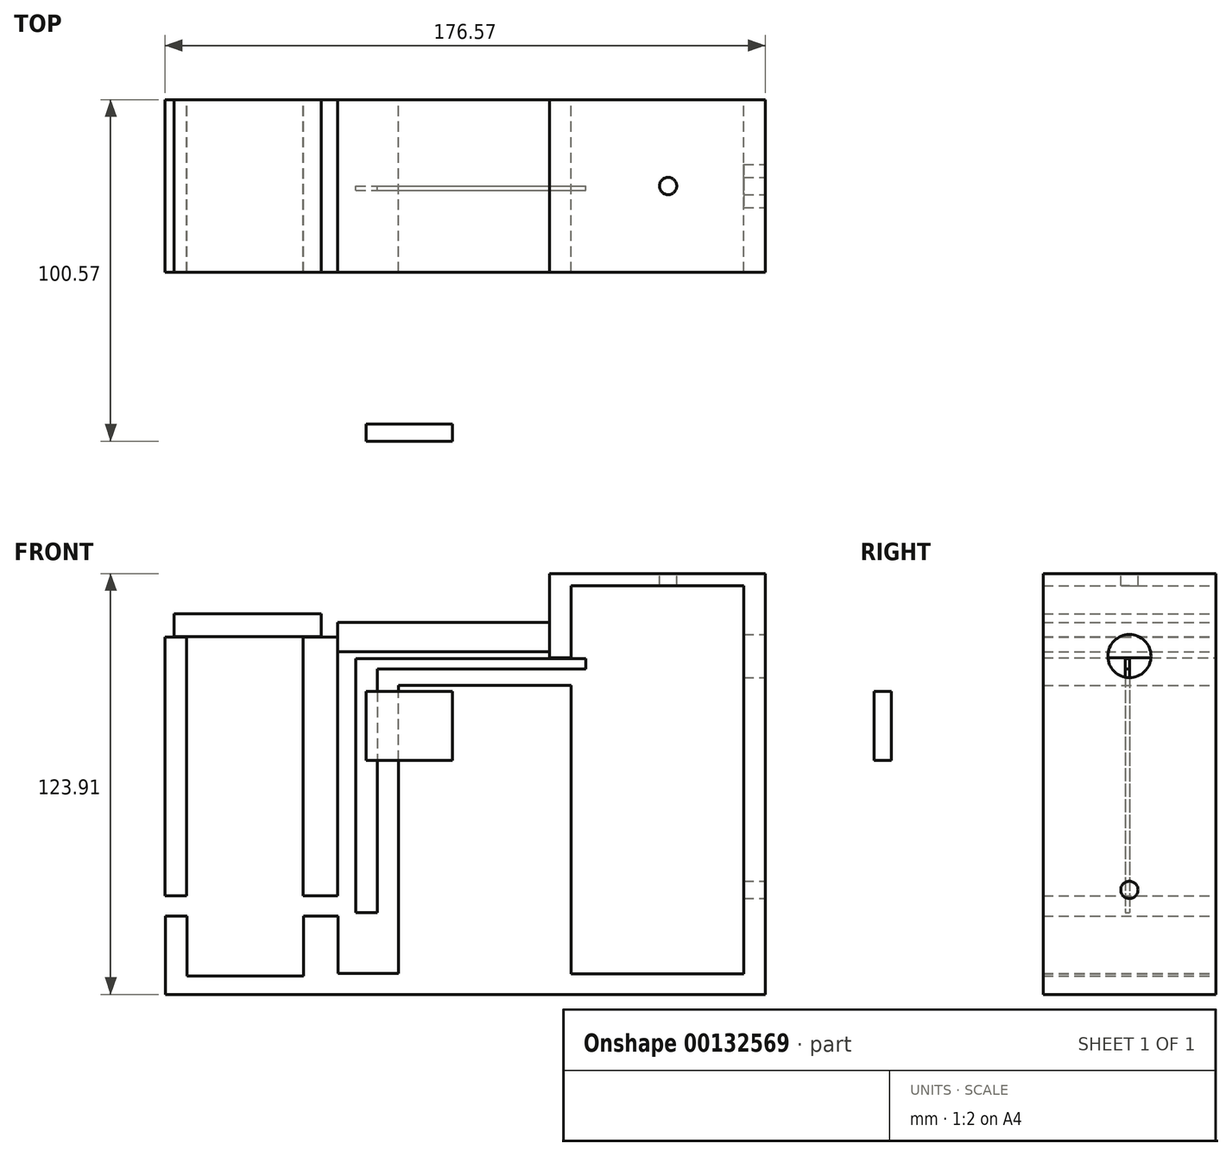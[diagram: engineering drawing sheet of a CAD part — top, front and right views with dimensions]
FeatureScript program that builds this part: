
annotation { "Feature Type Name" : "Feature", "Feature Type Description" : "" }
export const myFeature = defineFeature(function(context is Context, id is Id, definition is map)
    precondition{}
    {
        {
            var Q0;
            Q0=qCreatedBy(makeId("Front.planeOp"),FACE);
            var sketch = newSketch(context, id + "F0", { "sketchPlane" : qUnion([Q0])});
            skLineSegment(sketch, "E0.bottom", {"start": v(-59.08, 36.32) * mm, "end": v(-52.73, 36.32) * mm});
            skLineSegment(sketch, "E0.top", {"start": v(-59.08, -39.88) * mm, "end": v(-52.73, -39.88) * mm});
            skLineSegment(sketch, "E0.left", {"start": v(-59.08, 36.32) * mm, "end": v(-59.08, -39.88) * mm});
            skLineSegment(sketch, "E0.right", {"start": v(-52.73, 36.32) * mm, "end": v(-52.73, -39.88) * mm});
            skLineSegment(sketch, "E1.bottom", {"start": v(-18.44, 36.32) * mm, "end": v(-8.28, 36.32) * mm});
            skLineSegment(sketch, "E1.top", {"start": v(-18.44, -39.88) * mm, "end": v(-8.28, -39.88) * mm});
            skLineSegment(sketch, "E1.left", {"start": v(-18.44, 36.32) * mm, "end": v(-18.44, -39.88) * mm});
            skLineSegment(sketch, "E1.right", {"start": v(-8.28, 36.32) * mm, "end": v(-8.28, -39.88) * mm});
            skLineSegment(sketch, "E2.bottom", {"start": v(-59.04, -45.78) * mm, "end": v(-52.7, -45.78) * mm});
            skLineSegment(sketch, "E2.top", {"start": v(-59.04, -68.89) * mm, "end": v(-8.24, -68.89) * mm});
            skLineSegment(sketch, "E2.left", {"start": v(-59.04, -45.78) * mm, "end": v(-59.04, -68.89) * mm});
            skLineSegment(sketch, "E2.right", {"start": v(-8.24, -45.78) * mm, "end": v(-8.24, -62.7) * mm});
            skLineSegment(sketch, "E3.top", {"start": v(-52.7, -63.47) * mm, "end": v(-18.4, -63.47) * mm});
            skLineSegment(sketch, "E3.left", {"start": v(-52.7, -45.78) * mm, "end": v(-52.7, -63.47) * mm});
            skLineSegment(sketch, "E3.right", {"start": v(-18.4, -45.78) * mm, "end": v(-18.4, -63.47) * mm});
            skLineSegment(sketch, "E4.trimOffspring", {"start": v(-18.4, -45.78) * mm, "end": v(-8.24, -45.78) * mm});
            skLineSegment(sketch, "E5", {"start": v(-8.24, -62.7) * mm, "end": v(9.54, -62.7) * mm});
            skLineSegment(sketch, "E6", {"start": v(9.54, -62.7) * mm, "end": v(9.54, 22.1) * mm});
            skLineSegment(sketch, "E7", {"start": v(9.54, 22.1) * mm, "end": v(60.34, 22.1) * mm});
            skLineSegment(sketch, "E8", {"start": v(60.34, 22.1) * mm, "end": v(60.34, -62.87) * mm});
            skLineSegment(sketch, "E9", {"start": v(60.34, -68.89) * mm, "end": v(-8.24, -68.89) * mm});
            skLineSegment(sketch, "E10", {"start": v(60.34, -62.87) * mm, "end": v(111.14, -62.87) * mm});
            skLineSegment(sketch, "E11", {"start": v(111.14, -62.87) * mm, "end": v(111.14, 21.68) * mm});
            skLineSegment(sketch, "E12", {"start": v(111.14, 21.68) * mm, "end": v(111.14, 51.43) * mm});
            skLineSegment(sketch, "E13", {"start": v(111.14, 51.43) * mm, "end": v(60.34, 51.43) * mm});
            skLineSegment(sketch, "E14", {"start": v(60.34, 51.43) * mm, "end": v(60.34, 30.2) * mm});
            skLineSegment(sketch, "E15", {"start": v(60.34, 30.2) * mm, "end": v(53.99, 30.2) * mm});
            skLineSegment(sketch, "E16", {"start": v(53.99, 30.2) * mm, "end": v(53.99, 55.02) * mm});
            skLineSegment(sketch, "E17", {"start": v(53.99, 55.02) * mm, "end": v(117.49, 55.02) * mm});
            skLineSegment(sketch, "E18", {"start": v(117.49, 55.02) * mm, "end": v(117.49, -68.89) * mm});
            skLineSegment(sketch, "E19", {"start": v(117.49, -68.89) * mm, "end": v(60.34, -68.89) * mm});
            skSolve(sketch);
        }
        {
            var Q0;
            Q0=makeQuery(id+"F0.imprint","IMPRINT",FACE,{"disambiguationData":[TD([[makeQuery(id+"F0.imprint","IMPRINT",EDGE,{"derivedFrom":sQuery(id+"F0.wireOp",EDGE,"E0.bottom")}),-1.0]])]});
            var Q1;
            Q1=makeQuery(id+"F0.imprint","IMPRINT",FACE,{"disambiguationData":[TD([[makeQuery(id+"F0.imprint","IMPRINT",EDGE,{"derivedFrom":sQuery(id+"F0.wireOp",EDGE,"E1.bottom")}),-1.0]])]});
            var Q2;
            Q2=makeQuery(id+"F0.imprint","IMPRINT",FACE,{"disambiguationData":[TD([[makeQuery(id+"F0.imprint","IMPRINT",EDGE,{"derivedFrom":sQuery(id+"F0.wireOp",EDGE,"E2.bottom")}),-1.0]])]});
            extrude(context, id + "F1", {"entities" : qUnion([Q0, Q1, Q2]), "endBound" : BoundingType.SYMMETRIC, "depth" : 50.8 * mm});
        }
        {
            var Q0;
            Q0=makeQuery(id+"F1.opExtrude","SWEPT_FACE",FACE,{"disambiguationData":[OSD([sQuery(id+"F0.wireOp",EDGE,"E18")])]});
            var sketch = newSketch(context, id + "F2", { "sketchPlane" : qUnion([Q0])});
            skCircle(sketch, "E20", {"center": v(0, 30.75) * mm, "radius": 6.35 * mm});
            skSolve(sketch);
        }
        {
            var Q0;
            Q0=makeQuery(id+"F2.imprint","IMPRINT",FACE,{"disambiguationData":[TD([[makeQuery(id+"F2.imprint","IMPRINT",EDGE,{"derivedFrom":sQuery(id+"F2.wireOp",EDGE,"E20")}),1.0]])]});
            extrude(context, id + "F3", {"entities" : qUnion([Q0]), "operationType" : NewBodyOperationType.REMOVE, "oppositeDirection" : true, "depth" : 6.35 * mm});
        }
        {
            var Q0;
            Q0=makeQuery(id+"F1.opExtrude","SWEPT_FACE",FACE,{"disambiguationData":[OSD([sQuery(id+"F0.wireOp",EDGE,"E18")])]});
            var sketch = newSketch(context, id + "F4", { "sketchPlane" : qUnion([Q0])});
            skCircle(sketch, "E21", {"center": v(0, -38.1) * mm, "radius": 2.54 * mm});
            skSolve(sketch);
        }
        {
            var Q0;
            Q0=makeQuery(id+"F4.imprint","IMPRINT",FACE,{"disambiguationData":[TD([[makeQuery(id+"F4.imprint","IMPRINT",EDGE,{"derivedFrom":sQuery(id+"F4.wireOp",EDGE,"E21")}),1.0]])]});
            extrude(context, id + "F5", {"entities" : qUnion([Q0]), "operationType" : NewBodyOperationType.REMOVE, "oppositeDirection" : true, "depth" : 6.35 * mm});
        }
        {
            var Q0;
            Q0=makeQuery(id+"F1.opExtrude","SWEPT_FACE",FACE,{"disambiguationData":[OSD([sQuery(id+"F0.wireOp",EDGE,"E17")])]});
            var sketch = newSketch(context, id + "F6", { "sketchPlane" : qUnion([Q0])});
            skCircle(sketch, "E22", {"center": v(88.91, 0) * mm, "radius": 2.54 * mm});
            skSolve(sketch);
        }
        {
            var Q0;
            Q0=makeQuery(id+"F6.imprint","IMPRINT",FACE,{"disambiguationData":[TD([[makeQuery(id+"F6.imprint","IMPRINT",EDGE,{"derivedFrom":sQuery(id+"F6.wireOp",EDGE,"E22")}),1.0]])]});
            var Q1;
            Q1=sQuery(id+"F6.wireOp",EDGE,"E22");
            extrude(context, id + "F7", {"entities" : qUnion([Q0]), "operationType" : NewBodyOperationType.REMOVE, "surfaceEntities" : qUnion([Q1]), "oppositeDirection" : true, "depth" : 3.81 * mm});
        }
        {
            var Q0;
            Q0=qCreatedBy(makeId("Front.planeOp"),FACE);
            var sketch = newSketch(context, id + "F8", { "sketchPlane" : qUnion([Q0])});
            skLineSegment(sketch, "E23.bottom", {"start": v(-8.28, 40.66) * mm, "end": v(53.99, 40.66) * mm});
            skLineSegment(sketch, "E23.top", {"start": v(-8.28, 31.99) * mm, "end": v(53.99, 31.99) * mm});
            skLineSegment(sketch, "E23.left", {"start": v(-8.28, 40.66) * mm, "end": v(-8.28, 31.99) * mm});
            skLineSegment(sketch, "E23.right", {"start": v(53.99, 40.66) * mm, "end": v(53.99, 31.99) * mm});
            skSolve(sketch);
        }
        {
            var Q0;
            Q0=makeQuery(id+"F8.imprint","IMPRINT",FACE,{"disambiguationData":[TD([[makeQuery(id+"F8.imprint","IMPRINT",EDGE,{"derivedFrom":sQuery(id+"F8.wireOp",EDGE,"E23.bottom")}),-1.0]])]});
            extrude(context, id + "F9", {"entities" : qUnion([Q0]), "endBound" : BoundingType.SYMMETRIC, "depth" : 50.8 * mm});
        }
        {
            var Q0;
            Q0=qCreatedBy(makeId("Front.planeOp"),FACE);
            var sketch = newSketch(context, id + "F10", { "sketchPlane" : qUnion([Q0])});
            skLineSegment(sketch, "E24.bottom", {"start": v(-56.52, 43.27) * mm, "end": v(-13.17, 43.27) * mm});
            skLineSegment(sketch, "E24.top", {"start": v(-56.52, 36.53) * mm, "end": v(-13.17, 36.53) * mm});
            skLineSegment(sketch, "E24.left", {"start": v(-56.52, 43.27) * mm, "end": v(-56.52, 36.53) * mm});
            skLineSegment(sketch, "E24.right", {"start": v(-13.17, 43.27) * mm, "end": v(-13.17, 36.53) * mm});
            skSolve(sketch);
        }
        {
            var Q0;
            Q0=makeQuery(id+"F10.imprint","IMPRINT",FACE,{"disambiguationData":[TD([[makeQuery(id+"F10.imprint","IMPRINT",EDGE,{"derivedFrom":sQuery(id+"F10.wireOp",EDGE,"E24.bottom")}),-1.0]])]});
            extrude(context, id + "F11", {"entities" : qUnion([Q0]), "endBound" : BoundingType.SYMMETRIC, "depth" : 50.8 * mm});
        }
        {
            var Q0;
            Q0=qCreatedBy(makeId("Right.planeOp"),FACE);
            var sketch = newSketch(context, id + "F12", { "sketchPlane" : qUnion([Q0])});
            skLineSegment(sketch, "E25.bottom", {"start": v(-70.09, 20.32) * mm, "end": v(-75.17, 20.32) * mm});
            skLineSegment(sketch, "E25.top", {"start": v(-70.09, 0) * mm, "end": v(-75.17, 0) * mm});
            skLineSegment(sketch, "E25.left", {"start": v(-70.09, 20.32) * mm, "end": v(-70.09, 0) * mm});
            skLineSegment(sketch, "E25.right", {"start": v(-75.17, 20.32) * mm, "end": v(-75.17, 0) * mm});
            skSolve(sketch);
        }
        {
            var Q0;
            Q0=makeQuery(id+"F12.imprint","IMPRINT",FACE,{"disambiguationData":[TD([[makeQuery(id+"F12.imprint","IMPRINT",EDGE,{"derivedFrom":sQuery(id+"F12.wireOp",EDGE,"E25.bottom")}),1.0]])]});
            extrude(context, id + "F13", {"entities" : qUnion([Q0]), "depth" : 25.4 * mm});
        }
        {
            var Q0;
            Q0=qCreatedBy(makeId("Front.planeOp"),FACE);
            var sketch = newSketch(context, id + "F14", { "sketchPlane" : qUnion([Q0])});
            skLineSegment(sketch, "E26.top", {"start": v(-3.03, -44.82) * mm, "end": v(3.38, -44.82) * mm});
            skLineSegment(sketch, "E26.left", {"start": v(-3.03, 26.98) * mm, "end": v(-3.03, -44.82) * mm});
            skLineSegment(sketch, "E26.right", {"start": v(3.38, 26.98) * mm, "end": v(3.38, -44.82) * mm});
            skLineSegment(sketch, "E27.bottom", {"start": v(-3.03, 29.97) * mm, "end": v(64.7, 29.97) * mm});
            skLineSegment(sketch, "E27.top", {"start": v(3.38, 26.98) * mm, "end": v(64.7, 26.98) * mm});
            skLineSegment(sketch, "E27.left", {"start": v(-3.03, 29.97) * mm, "end": v(-3.03, 26.98) * mm});
            skLineSegment(sketch, "E27.right", {"start": v(64.7, 29.97) * mm, "end": v(64.7, 26.98) * mm});
            skSolve(sketch);
        }
        {
            var Q0;
            Q0=makeQuery(id+"F14.imprint","IMPRINT",FACE,{"disambiguationData":[TD([[makeQuery(id+"F14.imprint","IMPRINT",EDGE,{"derivedFrom":sQuery(id+"F14.wireOp",EDGE,"E26.top")}),1.0]])]});
            extrude(context, id + "F15", {"entities" : qUnion([Q0]), "depth" : 1.27 * mm});
        }
    });
